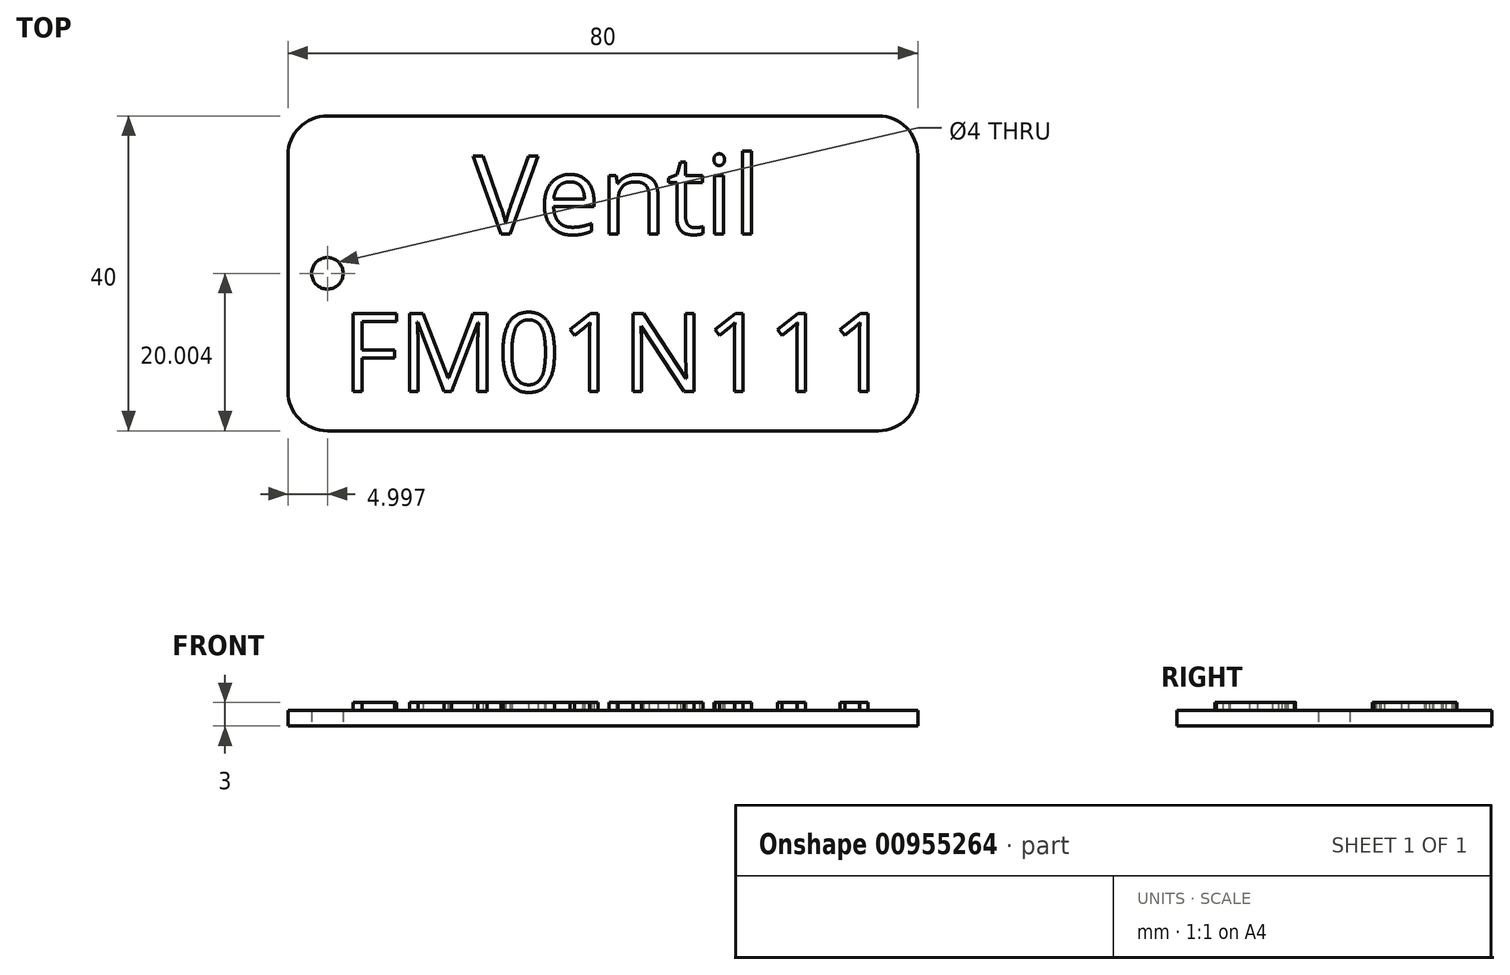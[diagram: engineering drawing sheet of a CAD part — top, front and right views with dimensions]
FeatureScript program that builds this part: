
annotation { "Feature Type Name" : "Feature", "Feature Type Description" : "" }
export const myFeature = defineFeature(function(context is Context, id is Id, definition is map)
    precondition{}
    {
        {
            var Q0;
            Q0=qCreatedBy(makeId("Top.planeOp"),FACE);
            var sketch = newSketch(context, id + "F0", { "sketchPlane" : qUnion([Q0])});
            skLineSegment(sketch, "E0.bottom", {"start": v(-37.1, 21.3) * mm, "end": v(32.9, 21.3) * mm});
            skLineSegment(sketch, "E0.top", {"start": v(-37.1, -18.7) * mm, "end": v(32.9, -18.7) * mm});
            skLineSegment(sketch, "E0.left", {"start": v(-42.1, 16.3) * mm, "end": v(-42.1, -13.7) * mm});
            skLineSegment(sketch, "E0.right", {"start": v(37.9, 16.3) * mm, "end": v(37.9, -13.7) * mm});
            skPoint(sketch, "E1.visualSharp", {"position": v(37.9, 21.3) * mm});
            skArc(sketch, "E1.filletArc", {"start": v(37.9, 16.3) * mm, "mid": v(36.44, 19.84) * mm, "end": v(32.9, 21.3) * mm});
            skPoint(sketch, "E2.visualSharp", {"position": v(37.9, -18.7) * mm});
            skArc(sketch, "E2.filletArc", {"start": v(32.9, -18.7) * mm, "mid": v(36.44, -17.23) * mm, "end": v(37.9, -13.7) * mm});
            skPoint(sketch, "E3.visualSharp", {"position": v(-42.1, -18.7) * mm});
            skArc(sketch, "E3.filletArc", {"start": v(-42.1, -13.7) * mm, "mid": v(-40.63, -17.23) * mm, "end": v(-37.1, -18.7) * mm});
            skPoint(sketch, "E4.visualSharp", {"position": v(-42.1, 21.3) * mm});
            skArc(sketch, "E4.filletArc", {"start": v(-37.1, 21.3) * mm, "mid": v(-40.63, 19.84) * mm, "end": v(-42.1, 16.3) * mm});
            skLineSegment(sketch, "E5", {"start": v(-42.1, 16.3) * mm, "end": v(37.9, 16.3) * mm, "construction": true});
            skLineSegment(sketch, "E6", {"start": v(-42.1, -13.7) * mm, "end": v(37.9, -13.7) * mm, "construction": true});
            skLineSegment(sketch, "E7", {"start": v(32.9, 21.3) * mm, "end": v(32.9, -18.7) * mm, "construction": true});
            skLineSegment(sketch, "E8", {"start": v(-37.1, 21.3) * mm, "end": v(-37.1, -18.7) * mm, "construction": true});
            skLineSegment(sketch, "E9", {"start": v(-42.1, 1.3) * mm, "end": v(37.9, 1.3) * mm, "construction": true});
            skCircle(sketch, "E10", {"center": v(-37.1, 1.3) * mm, "radius": 2 * mm});
            skSolve(sketch);
        }
        {
            var Q0;
            Q0 = qSketchRegion(id + "F0", true);
            extrude(context, id + "F1", {"entities" : qUnion([Q0]), "depth" : 2 * mm, "offsetDistance" : 25 * mm});
        }
        {
            var Q0;
            Q0=makeQuery(id+"F1.opExtrude","CAP_FACE",FACE,{"disambiguationData":[OSD([sQuery(id+"F0.wireOp",EDGE,"E0.bottom"),sQuery(id+"F0.wireOp",EDGE,"E0.top"),sQuery(id+"F0.wireOp",EDGE,"E0.left"),sQuery(id+"F0.wireOp",EDGE,"E0.right"),sQuery(id+"F0.wireOp",EDGE,"E1.filletArc"),sQuery(id+"F0.wireOp",EDGE,"E2.filletArc"),sQuery(id+"F0.wireOp",EDGE,"E3.filletArc"),sQuery(id+"F0.wireOp",EDGE,"E4.filletArc"),sQuery(id+"F0.wireOp",EDGE,"E10")])],"isStart":false});
            var sketch = newSketch(context, id + "F2", { "sketchPlane" : qUnion([Q0])});
            skLineSegment(sketch, "E11", {"start": v(-42.1, -13.7) * mm, "end": v(37.9, -13.7) * mm, "construction": true});
            skLineSegment(sketch, "E12", {"start": v(-42.1, 16.3) * mm, "end": v(37.9, 16.3) * mm, "construction": true});
            skLineSegment(sketch, "E13", {"start": v(-42.1, 1.3) * mm, "end": v(37.9, 1.3) * mm, "construction": true});
            skLineSegment(sketch, "E14.0", {"start": v(-42.1, 1.26) * mm, "end": v(37.9, 1.26) * mm, "construction": true});
            skLineSegment(sketch, "E15.0", {"start": v(-42.1, 6.3) * mm, "end": v(37.9, 6.3) * mm, "construction": true});
            skLineSegment(sketch, "E16.0", {"start": v(-42.1, -3.7) * mm, "end": v(37.9, -3.7) * mm, "construction": true});
            skText(sketch, "E17", { "text": "Ventil", "fontName": "OpenSans-Regular.ttf"});
            skText(sketch, "E18", { "text": "FM01N111", "fontName": "OpenSans-Regular.ttf"});
            const initialGuessF2  = {"E17": [-0.01857, 0.0063, 1, 0, 0.01], "E18": [-0.03519, -0.0137, 1, 0, 0.01]};
            skSetInitialGuess(sketch, initialGuessF2);
            skSolve(sketch);
        }
        {
            var Q0;
            Q0 = qSketchRegion(id + "F2", true);
            extrude(context, id + "F3", {"entities" : qUnion([Q0]), "operationType" : NewBodyOperationType.ADD, "depth" : 1 * mm, "offsetDistance" : 25 * mm});
        }
    });
